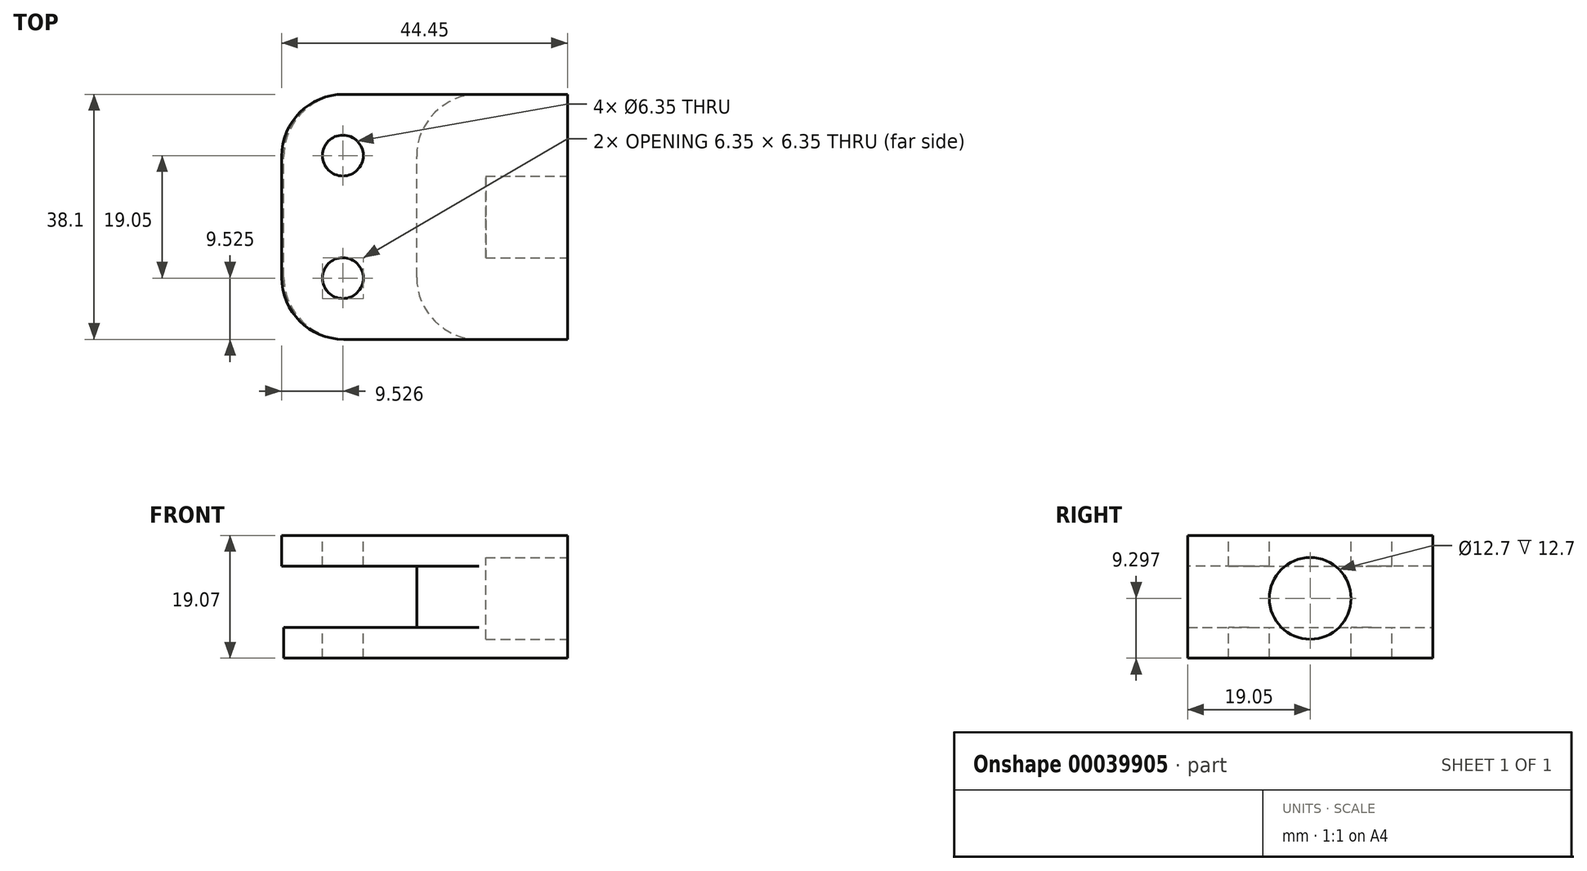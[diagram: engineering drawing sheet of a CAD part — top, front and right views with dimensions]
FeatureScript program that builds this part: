
annotation { "Feature Type Name" : "Feature", "Feature Type Description" : "" }
export const myFeature = defineFeature(function(context is Context, id is Id, definition is map)
    precondition{}
    {
        {
            var Q0;
            Q0=qCreatedBy(makeId("Front.planeOp"),FACE);
            var sketch = newSketch(context, id + "F0", { "sketchPlane" : qUnion([Q0])});
            skLineSegment(sketch, "E0", {"start": v(16.25, -5.85) * mm, "end": v(16.25, 13.2) * mm});
            skLineSegment(sketch, "E1", {"start": v(16.25, 13.2) * mm, "end": v(-28.2, 13.2) * mm});
            skLineSegment(sketch, "E2", {"start": v(-28.2, 8.43) * mm, "end": v(-7.2, 8.43) * mm});
            skLineSegment(sketch, "E3", {"start": v(-7.2, 8.43) * mm, "end": v(-7.2, -1.1) * mm});
            skLineSegment(sketch, "E4", {"start": v(-7.2, -1.1) * mm, "end": v(-27.85, -1.1) * mm});
            skLineSegment(sketch, "E5", {"start": v(-27.85, -1.1) * mm, "end": v(-27.85, -5.87) * mm});
            skLineSegment(sketch, "E6", {"start": v(-28.2, 13.2) * mm, "end": v(-28.2, 8.43) * mm});
            skLineSegment(sketch, "E7", {"start": v(-27.85, -5.87) * mm, "end": v(16.25, -5.85) * mm});
            skSolve(sketch);
        }
        {
            var Q0;
            Q0=makeQuery(id+"F0.imprint","IMPRINT",FACE,{"disambiguationData":[TD([[makeQuery(id+"F0.imprint","IMPRINT",EDGE,{"derivedFrom":sQuery(id+"F0.wireOp",EDGE,"E0")}),1.0]])]});
            extrude(context, id + "F1", {"entities" : qUnion([Q0]), "depth" : 38.1 * mm});
        }
        {
            var Q0;
            Q0=makeQuery(id+"F1.opExtrude","SWEPT_FACE",FACE,{"disambiguationData":[OSD([sQuery(id+"F0.wireOp",EDGE,"E1")])]});
            var sketch = newSketch(context, id + "F2", { "sketchPlane" : qUnion([Q0])});
            skCircle(sketch, "E8", {"center": v(-18.67, -9.53) * mm, "radius": 3.18 * mm});
            skCircle(sketch, "E9", {"center": v(-18.67, -28.58) * mm, "radius": 3.18 * mm});
            skSolve(sketch);
        }
        {
            var Q0;
            Q0=makeQuery(id+"F2.imprint","IMPRINT",FACE,{"disambiguationData":[TD([[makeQuery(id+"F2.imprint","IMPRINT",EDGE,{"derivedFrom":sQuery(id+"F2.wireOp",EDGE,"E9")}),1.0]])]});
            var Q1;
            Q1=makeQuery(id+"F2.imprint","IMPRINT",FACE,{"disambiguationData":[TD([[makeQuery(id+"F2.imprint","IMPRINT",EDGE,{"derivedFrom":sQuery(id+"F2.wireOp",EDGE,"E8")}),1.0]])]});
            extrude(context, id + "F3", {"entities" : qUnion([Q0, Q1]), "operationType" : NewBodyOperationType.REMOVE, "oppositeDirection" : true, "depth" : 38.1 * mm});
        }
        {
            var Q0;
            Q0=makeQuery(id+"F1.opExtrude","SWEPT_FACE",FACE,{"disambiguationData":[OSD([sQuery(id+"F0.wireOp",EDGE,"E0")])]});
            var sketch = newSketch(context, id + "F4", { "sketchPlane" : qUnion([Q0])});
            skCircle(sketch, "E10", {"center": v(-19.05, 3.43) * mm, "radius": 6.35 * mm});
            skPoint(sketch, "E10.centerSnap0", {"position": v(-19.05, -5.85) * mm});
            skSolve(sketch);
        }
        {
            var Q0;
            Q0=makeQuery(id+"F4.imprint","IMPRINT",FACE,{"disambiguationData":[TD([[makeQuery(id+"F4.imprint","IMPRINT",EDGE,{"derivedFrom":sQuery(id+"F4.wireOp",EDGE,"E10")}),1.0]])]});
            extrude(context, id + "F5", {"entities" : qUnion([Q0]), "operationType" : NewBodyOperationType.REMOVE, "oppositeDirection" : true, "depth" : 12.7 * mm});
        }
        {
            var Q0;
            Q0=makeQuery(id+"F1.opExtrude","CAP_EDGE",EDGE,{"disambiguationData":[OSD([sQuery(id+"F0.wireOp",EDGE,"E6")])],"isStart":false});
            var Q1;
            Q1=makeQuery(id+"F1.opExtrude","CAP_EDGE",EDGE,{"disambiguationData":[OSD([sQuery(id+"F0.wireOp",EDGE,"E6")])],"isStart":true});
            var Q2;
            Q2=makeQuery(id+"F1.opExtrude","CAP_EDGE",EDGE,{"disambiguationData":[OSD([sQuery(id+"F0.wireOp",EDGE,"E5")])],"isStart":true});
            var Q3;
            Q3=makeQuery(id+"F1.opExtrude","CAP_EDGE",EDGE,{"disambiguationData":[OSD([sQuery(id+"F0.wireOp",EDGE,"E5")])],"isStart":false});
            var Q4;
            Q4=makeQuery(id+"F1.opExtrude","CAP_EDGE",EDGE,{"disambiguationData":[OSD([sQuery(id+"F0.wireOp",EDGE,"E3")])],"isStart":false});
            var Q5;
            Q5=makeQuery(id+"F1.opExtrude","CAP_EDGE",EDGE,{"disambiguationData":[OSD([sQuery(id+"F0.wireOp",EDGE,"E3")])],"isStart":true});
            fillet(context, id + "F6", {"entities" : qUnion([Q0, Q1, Q2, Q3, Q4, Q5]), "radius" : 9.65 * mm, "tangentPropagation" : true, "allowEdgeOverflow" : false});
        }
    });
